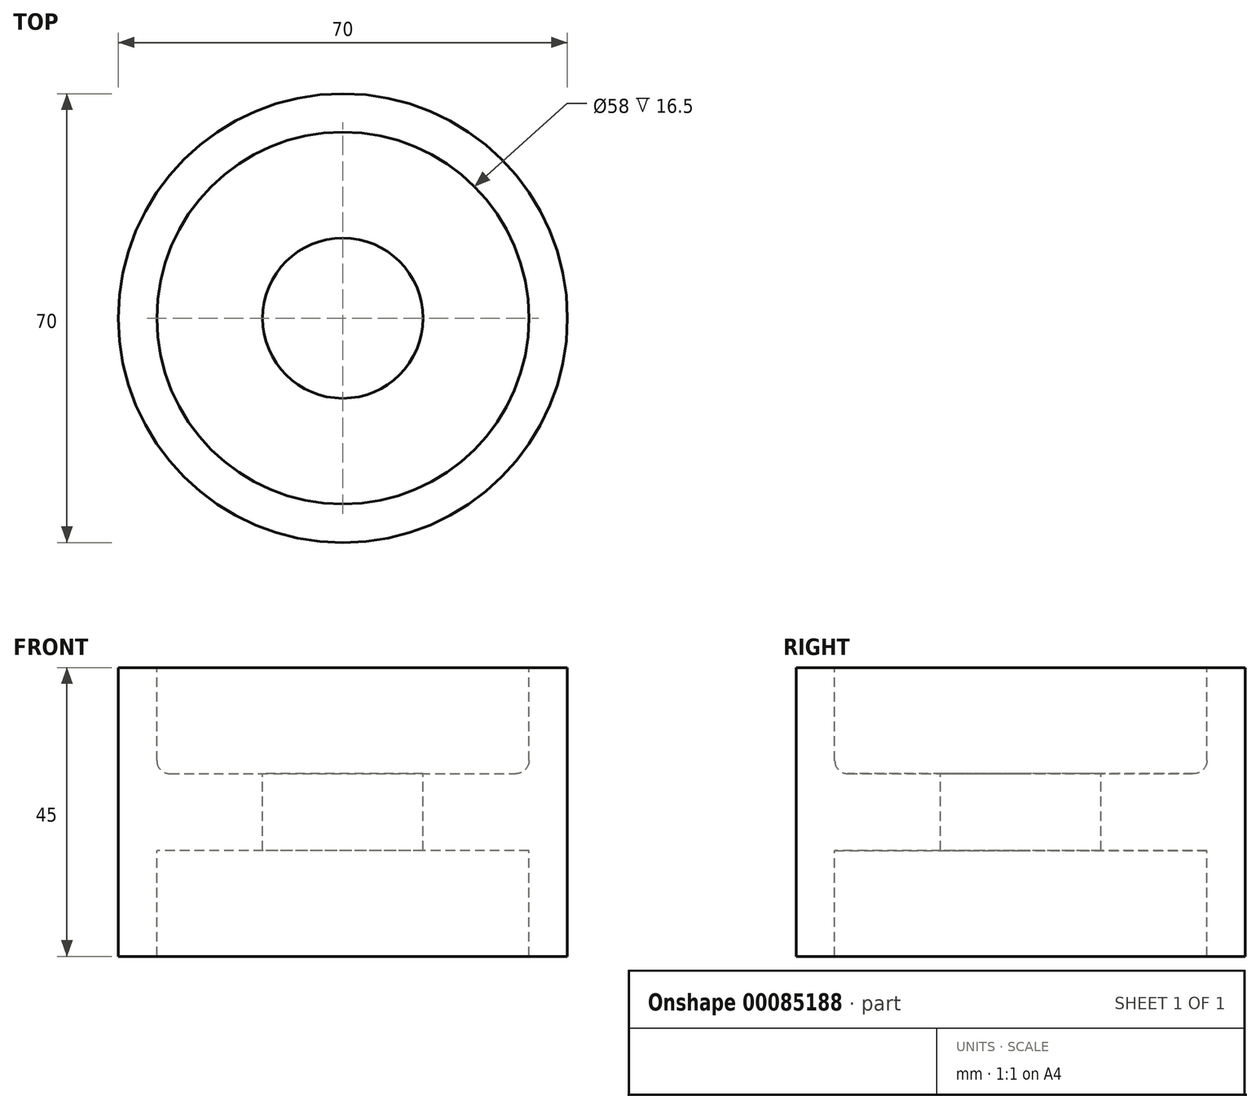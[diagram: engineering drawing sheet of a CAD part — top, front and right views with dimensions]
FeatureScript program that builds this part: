
annotation { "Feature Type Name" : "Feature", "Feature Type Description" : "" }
export const myFeature = defineFeature(function(context is Context, id is Id, definition is map)
    precondition{}
    {
        {
            var Q0;
            Q0=qCreatedBy(makeId("Front.planeOp"),FACE);
            var sketch = newSketch(context, id + "F0", { "sketchPlane" : qUnion([Q0])});
            skLineSegment(sketch, "E0", {"start": v(0, 170.78) * mm, "end": v(0, -146.63) * mm, "construction": true});
            skLineSegment(sketch, "E1.bottom", {"start": v(29, 22.5) * mm, "end": v(35, 22.5) * mm});
            skLineSegment(sketch, "E1.top", {"start": v(29, -22.5) * mm, "end": v(35, -22.5) * mm});
            skLineSegment(sketch, "E1.left", {"start": v(29, 22.5) * mm, "end": v(29, -22.5) * mm});
            skLineSegment(sketch, "E1.right", {"start": v(35, 22.5) * mm, "end": v(35, -22.5) * mm});
            skSolve(sketch);
        }
        {
            var Q0;
            Q0 = qSketchRegion(id + "F0", true);
            var Q1;
            Q1=sQuery(id+"F0.wireOp",EDGE,"E0");
            revolve(context, id + "F1", {"entities" : qUnion([Q0]), "axis" : qUnion([Q1]), "revolveType" : RevolveType.FULL});
        }
        {
            var Q0;
            Q0=qCreatedBy(makeId("Front.planeOp"),FACE);
            var sketch = newSketch(context, id + "F2", { "sketchPlane" : qUnion([Q0])});
            skLineSegment(sketch, "E2", {"start": v(29, 6) * mm, "end": v(29, -6) * mm});
            skLineSegment(sketch, "E3", {"start": v(29, 6) * mm, "end": v(12.5, 6) * mm});
            skLineSegment(sketch, "E4", {"start": v(12.5, 6) * mm, "end": v(12.5, -6) * mm});
            skLineSegment(sketch, "E5", {"start": v(12.5, -6) * mm, "end": v(29, -6) * mm});
            skLineSegment(sketch, "E6", {"start": v(0, 124.56) * mm, "end": v(0, -118.26) * mm, "construction": true});
            skSolve(sketch);
        }
        {
            var Q0;
            Q0=makeQuery(id+"F2.imprint","IMPRINT",FACE,{"disambiguationData":[TD([[makeQuery(id+"F2.imprint","IMPRINT",EDGE,{"derivedFrom":sQuery(id+"F2.wireOp",EDGE,"E2")}),-1.0]])]});
            var Q1;
            Q1=sQuery(id+"F2.wireOp",EDGE,"E6");
            revolve(context, id + "F3", {"operationType" : NewBodyOperationType.ADD, "entities" : qUnion([Q0]), "axis" : qUnion([Q1]), "revolveType" : RevolveType.FULL});
        }
        {
            var Q0;
            Q0=makeQuery(id+"F3.opRevolve","SWEPT_EDGE",EDGE,{"disambiguationData":[OSD([sQuery(id+"F2.wireOp",EDGE,"E2"),sQuery(id+"F2.wireOp",EDGE,"E3")])]});
            var Q1;
            Q1=makeQuery(id+"F3.opRevolve","SWEPT_EDGE",EDGE,{"disambiguationData":[OSD([sQuery(id+"F2.wireOp",EDGE,"E2"),sQuery(id+"F2.wireOp",EDGE,"E5")])]});
            fillet(context, id + "F4", {"entities" : qUnion([Q0, Q1]), "radius" : 2 * mm, "tangentPropagation" : true, "allowEdgeOverflow" : false});
        }
        {
            var Q0;
            Q0=qCreatedBy(makeId("Front.planeOp"),FACE);
            var sketch = newSketch(context, id + "F5", { "sketchPlane" : qUnion([Q0])});
            skLineSegment(sketch, "E7", {"start": v(94.1, 0) * mm, "end": v(-101.28, 0) * mm, "construction": true});
            skSolve(sketch);
        }
    });
